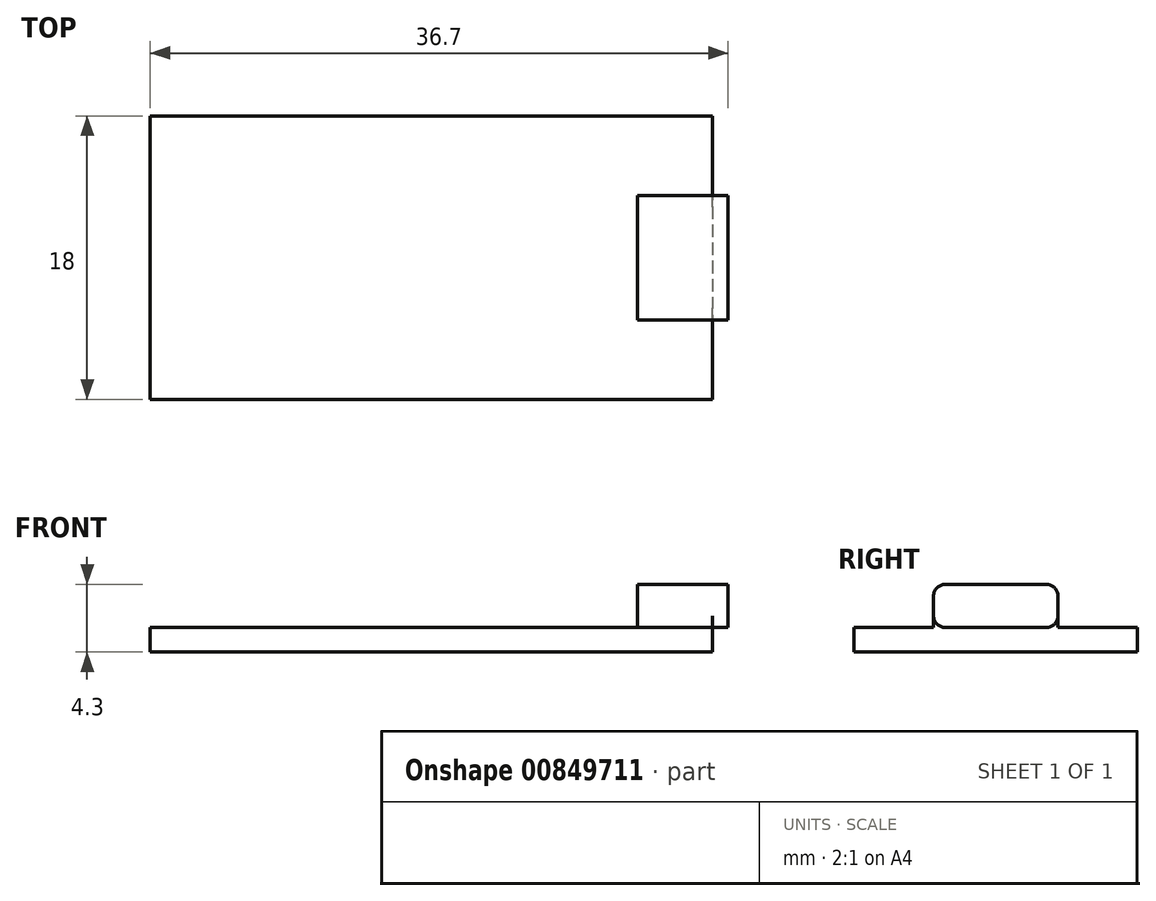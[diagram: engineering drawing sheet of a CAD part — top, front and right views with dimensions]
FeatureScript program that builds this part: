
annotation { "Feature Type Name" : "Feature", "Feature Type Description" : "" }
export const myFeature = defineFeature(function(context is Context, id is Id, definition is map)
    precondition{}
    {
        {
            var Q0;
            Q0=qCreatedBy(makeId("Top.planeOp"),FACE);
            var sketch = newSketch(context, id + "F0", { "sketchPlane" : qUnion([Q0])});
            skLineSegment(sketch, "E0.bottom", {"start": v(17.85, 9) * mm, "end": v(-17.85, 9) * mm});
            skLineSegment(sketch, "E0.top", {"start": v(17.85, -9) * mm, "end": v(-17.85, -9) * mm});
            skLineSegment(sketch, "E0.left", {"start": v(17.85, 9) * mm, "end": v(17.85, -9) * mm});
            skLineSegment(sketch, "E0.right", {"start": v(-17.85, 9) * mm, "end": v(-17.85, -9) * mm});
            skPoint(sketch, "E0.middle", {"position": v(0, 0) * mm});
            skSolve(sketch);
        }
        {
            var Q0;
            Q0=makeQuery(id+"F0.imprint","IMPRINT",FACE,{"disambiguationData":[TD([[makeQuery(id+"F0.imprint","IMPRINT",EDGE,{"derivedFrom":sQuery(id+"F0.wireOp",EDGE,"E0.bottom")}),1.0]])]});
            extrude(context, id + "F1", {"entities" : qUnion([Q0]), "depth" : 1.55 * mm, "offsetDistance" : 25 * mm});
        }
        {
            var Q0;
            Q0=makeQuery(id+"F1.opExtrude","CAP_FACE",FACE,{"disambiguationData":[OSD([sQuery(id+"F0.wireOp",EDGE,"E0.bottom"),sQuery(id+"F0.wireOp",EDGE,"E0.top"),sQuery(id+"F0.wireOp",EDGE,"E0.left"),sQuery(id+"F0.wireOp",EDGE,"E0.right")])],"isStart":false});
            var sketch = newSketch(context, id + "F2", { "sketchPlane" : qUnion([Q0])});
            skLineSegment(sketch, "E1.bottom", {"start": v(18.85, 3.95) * mm, "end": v(13.1, 3.95) * mm});
            skLineSegment(sketch, "E1.top", {"start": v(18.85, -3.95) * mm, "end": v(13.1, -3.95) * mm});
            skLineSegment(sketch, "E1.left", {"start": v(18.85, 3.95) * mm, "end": v(18.85, -3.95) * mm});
            skLineSegment(sketch, "E1.right", {"start": v(13.1, 3.95) * mm, "end": v(13.1, -3.95) * mm});
            skPoint(sketch, "E1.middle", {"position": v(15.98, 0) * mm});
            skSolve(sketch);
        }
        {
            var Q0;
            Q0 = qSketchRegion(id + "F2", true);
            extrude(context, id + "F3", {"entities" : qUnion([Q0]), "operationType" : NewBodyOperationType.ADD, "depth" : 2.75 * mm, "offsetDistance" : 25 * mm});
        }
        {
            var Q0;
            Q0=makeQuery(id+"F3.opExtrude","CAP_EDGE",EDGE,{"disambiguationData":[OSD([sQuery(id+"F2.wireOp",EDGE,"E1.bottom")])],"isStart":false});
            var Q1;
            Q1=makeQuery(id+"F3.opExtrude","CAP_EDGE",EDGE,{"disambiguationData":[OSD([sQuery(id+"F2.wireOp",EDGE,"E1.top")])],"isStart":false});
            var Q2;
            {var subQ0=sQuery(id+"F2.wireOp",EDGE,"E1.bottom");Q2=makeQuery(id+"F3.boolean.opBoolean","SPLIT",EDGE,{"disambiguationData":[topologyDisambiguationEdgeConnected([makeQuery(id+"F3.opExtrude","CAP_FACE",FACE,{"disambiguationData":[OSD([subQ0,sQuery(id+"F2.wireOp",EDGE,"E1.top"),sQuery(id+"F2.wireOp",EDGE,"E1.left"),sQuery(id+"F2.wireOp",EDGE,"E1.right")])],"isStart":true})])],"derivedFrom":makeQuery(id+"F3.opExtrude","CAP_EDGE",EDGE,{"disambiguationData":[OSD([subQ0])],"isStart":true})});}
            var Q3;
            {var subQ0=sQuery(id+"F2.wireOp",EDGE,"E1.top");Q3=makeQuery(id+"F3.boolean.opBoolean","SPLIT",EDGE,{"disambiguationData":[topologyDisambiguationEdgeConnected([makeQuery(id+"F3.opExtrude","CAP_FACE",FACE,{"disambiguationData":[OSD([sQuery(id+"F2.wireOp",EDGE,"E1.bottom"),subQ0,sQuery(id+"F2.wireOp",EDGE,"E1.left"),sQuery(id+"F2.wireOp",EDGE,"E1.right")])],"isStart":true})])],"derivedFrom":makeQuery(id+"F3.opExtrude","CAP_EDGE",EDGE,{"disambiguationData":[OSD([subQ0])],"isStart":true})});}
            fillet(context, id + "F4", {"entities" : qUnion([Q0, Q1, Q2, Q3]), "radius" : .75 * mm, "tangentPropagation" : true, "allowEdgeOverflow" : false});
        }
    });
